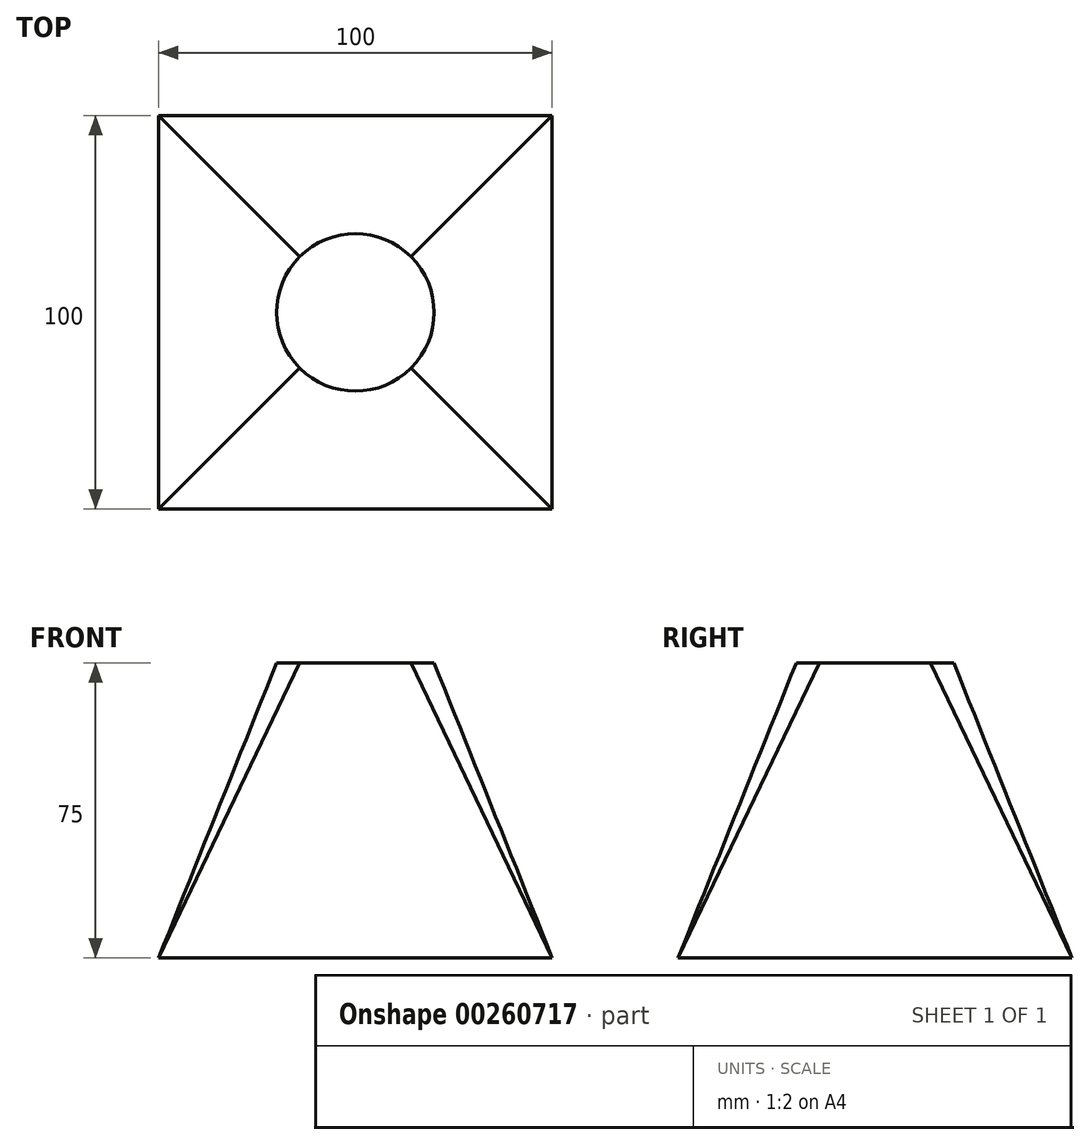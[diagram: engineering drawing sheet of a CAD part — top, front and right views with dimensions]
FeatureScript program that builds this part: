
annotation { "Feature Type Name" : "Feature", "Feature Type Description" : "" }
export const myFeature = defineFeature(function(context is Context, id is Id, definition is map)
    precondition{}
    {
        {
            var Q0;
            Q0=qCreatedBy(makeId("Top.planeOp"),FACE);
            var sketch = newSketch(context, id + "F0", { "sketchPlane" : qUnion([Q0])});
            skLineSegment(sketch, "E0.bottom", {"start": v(-50, 50) * mm, "end": v(50, 50) * mm});
            skLineSegment(sketch, "E0.top", {"start": v(-50, -50) * mm, "end": v(50, -50) * mm});
            skLineSegment(sketch, "E0.left", {"start": v(-50, 50) * mm, "end": v(-50, -50) * mm});
            skLineSegment(sketch, "E0.right", {"start": v(50, 50) * mm, "end": v(50, -50) * mm});
            skPoint(sketch, "E0.middle", {"position": v(0, 0) * mm});
            skSolve(sketch);
        }
        {
            var Q0;
            Q0=makeQuery(id+"F0.imprint","IMPRINT",FACE,{"disambiguationData":[TD([[makeQuery(id+"F0.imprint","IMPRINT",EDGE,{"derivedFrom":sQuery(id+"F0.wireOp",EDGE,"E0.bottom")}),-1.0]])]});
            cPlane(context, id + "F1", {"entities" : qUnion([Q0]), "cplaneType" : CPlaneType.OFFSET, "offset" : 75 * mm, "width" : 150 * mm, "height" : 150 * mm});
        }
        {
            var Q0;
            Q0=qCreatedBy(id+"F1.planeOp",FACE);
            var sketch = newSketch(context, id + "F2", { "sketchPlane" : qUnion([Q0])});
            skCircle(sketch, "E1", {"center": v(0, 0) * mm, "radius": 20 * mm});
            skSolve(sketch);
        }
        {
            var Q0;
            Q0=makeQuery(id+"F0.imprint","IMPRINT",FACE,{"disambiguationData":[TD([[makeQuery(id+"F0.imprint","IMPRINT",EDGE,{"derivedFrom":sQuery(id+"F0.wireOp",EDGE,"E0.bottom")}),-1.0]])]});
            var Q1;
            Q1=makeQuery(id+"F2.imprint","IMPRINT",FACE,{"disambiguationData":[TD([[makeQuery(id+"F2.imprint","IMPRINT",EDGE,{"derivedFrom":sQuery(id+"F2.wireOp",EDGE,"E1")}),1.0]])]});
            loft(context, id + "F3", {"sheetProfilesArray" : [{ "sheetProfileEntities" : qUnion([Q0]) }, { "sheetProfileEntities" : qUnion([Q1]) }]});
        }
    });
